# Revit family: EKF_EE_ПанельГоризонтальнаяДляСекционированияTrivia_AVERES
name_source: partatom
category: Электрооборудование
units: mm (PartAtom-declared; Revit-internal decimal feet)

## family parameters
Всегда вертикально = Нет
На основе рабочей плоскости = Да
Общий = Да
При загрузке вырезать с полостями = Нет
Размер круглого соединителя = Использовать диаметр
Тип детали = Силовой щит
Точка расчета площади = Нет

## types (15) — shared parameters
ADSK_Единица измерения = шт.
ADSK_Завод-изготовитель = EKF
ADSK_Количество = 1
ADSK_Материал = RAL 7035_Сталь
ADSK_Размер_Высота = 65 мм
Глубина = 400 мм
Изготовитель = EKF
Отметка по умолчанию = 1219.2 мм
Серия номенклатуры = Averes
Степень защиты IP = -
ТВ = EKF_2_TRIVIA_AVERES
Тип установки = -
Шаг_НабораПластронов_2шт = 100 мм
zero-valued in all types: ADSK_Масса

## per-type parameters (varying)
| type | ADSK_Код изделия | ADSK_Размер_Глубина | ADSK_Размер_Ширина | Тип |
| Панель горизонтальная для секционирования Ш200 Г400 мм EKF AVERES | PCH24 | 174 мм | 361.5 мм | 720 мм |
| Панель горизонтальная для секционирования Ш200 Г600 мм EKF AVERES | PCH26 | 174 мм | 561.5 мм | 721 мм |
| Панель горизонтальная для секционирования Ш200 Г800 мм EKF AVERES | PCH28 | 174 мм | 761.5 мм | 722 мм |
| Панель горизонтальная для секционирования Ш300 Г400 мм EKF AVERES | PCH34 | 223 мм | 361.5 мм | 723 мм |
| Панель горизонтальная для секционирования Ш300 Г600 мм EKF AVERES | PCH36 | 223 мм | 561.5 мм | 724 мм |
| Панель горизонтальная для секционирования Ш300 Г800 мм EKF AVERES | PCH38 | 223 мм | 761.5 мм | 725 мм |
| Панель горизонтальная для секционирования Ш400 Г400 мм EKF AVERES | PCH44 | 323 мм | 361.5 мм | 726 мм |
| Панель горизонтальная для секционирования Ш400 Г600 мм EKF AVERES | PCH46 | 323 мм | 561.5 мм | 727 мм |
| Панель горизонтальная для секционирования Ш400 Г800 мм EKF AVERES | PCH48 | 323 мм | 761.5 мм | 728 мм |
| Панель горизонтальная для секционирования Ш600 Г400 мм EKF AVERES | PCH64 | 523 мм | 361.5 мм | 729 мм |
| Панель горизонтальная для секционирования Ш600 Г600 мм EKF AVERES | PCH66 | 523 мм | 561.5 мм | 730 мм |
| Панель горизонтальная для секционирования Ш600 Г800 мм EKF AVERES | PCH68 | 523 мм | 761.5 мм | 731 мм |
| Панель горизонтальная для секционирования Ш800 Г400 мм EKF AVERES | PCH84 | 723 мм | 361.5 мм | 732 мм |
| Панель горизонтальная для секционирования Ш800 Г600 мм EKF AVERES | PCH86 | 723 мм | 561.5 мм | 733 мм |
| Панель горизонтальная для секционирования Ш800 Г800 мм EKF AVERES | PCH88 | 723 мм | 761.5 мм | 734 мм |

note: column(s) folded — value = type name in every type: ADSK_Марка, ADSK_Наименование, ADSK_Обозначение
